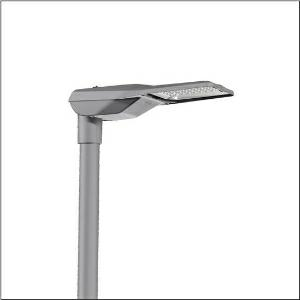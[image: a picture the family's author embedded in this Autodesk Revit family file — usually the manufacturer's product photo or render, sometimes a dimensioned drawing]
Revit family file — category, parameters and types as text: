
# Revit family: streetlight_sl_21_mini___st1_0a_5xe2d33s08gb_0caf
name_source: partatom
category: Lighting Fixtures
units: mm (PartAtom-declared; Revit-internal decimal feet)

## family parameters
Cut with Voids When Loaded = No
Host = Face
Light Source = No
Part Type = Normal
Room Calculation Point = No
Round Connector Dimension = Use Diameter
Shared = No

## types (1)
- --- (1 x LED, 5940 lm, 40.4 W, 3000K)
    Apparent Load = 40 VA
    CIE Flux Codes = 37 72 97 100 100
    Color Rendering = 70
    Color Temperature = 3000K
    Default Elevation = 1800 mm
    Description = Streetlight SL 21 mini, mast luminaire, primary light control with lens, of PMMA, primary optical cover: cover, of toughened safety glass, transparent, light distribution: ST1.0a, light emission: direct distribution, primary light characteristic: asymmetric, installation type: side-entry, post-top, LED, High Power LED, rated luminous flux: 5.940lm, luminous efficacy: 147lm/W, light colour: 730, colour temperature: 3000K, control gear: ECG Smart Interface, control: flexible luminous flux parameterisation, time-dependent luminous flux control, constant luminous flux control, overheat protection, mains connection: 220..240V, AC, 50/60Hz, start of lifetime: 40W, end of lifetime: 41W, reduction: 19W, luminaire housing, of diecast aluminium, powder-coated, Siteco® metallic grey (DB 702S), corrosivity category C5 according to DIN EN ISO 12944, length: 628mm, width: 235mm, height: 110mm, spigot size: 60/76mm (post-top) and 42/60/76mm (side-entry), mast flange for spigot size: 42mm: 5XC10008XM4, 60mm: 5XC10008XM2, 76/60mm: 5XC10108XM1, protection rating (complete): IP66, insulation class (complete): insulation class II (safety insulation), certification: CE, ENEC, VDE, impact resistance: IK09, permissible operating ambient temperature for outdoor applications: -40..+50°C, standard-compliant lighting for roads and squares, packaging unit: 1 piece

Light Distribution: ST1.0a
    Height = 110 mm
    Lamp = 1 x LED
    Lamp Light Flux = 5940 lm
    Lamp Power = 40.4 W
    Lamp count = 1
    Length = 625 mm
    Luminous efficacy = 147 lm/W
    Manufacturer = Siteco
    ModVariant = No
    Model = 5XE2D33S08GB
    Number of Poles = 1
    OnlyDefault = Yes
    Power Factor = 1
    Product Name = Streetlight SL 21 mini | ST1.0a
    Product group = mast luminaire | pylon top
    ProductGroupID = 6100
    Protection Class = Protection class II
    Protection Degree = IP 66
    RLX_Detail_Level = 1
    RlxData = <blob elided: 91809 chars, md5=dd1bda40>
    Socket = socket
    Standby Power = 0 W
    System Light Flux = 5940 lm
    System Power = 40 W
    Type Comments = factory setting: luminous flux: 100 % | dim-lin: 254 | 812 mA
    Type Image = l_1003515.jpg
    URL = http://relux.com
    VarID = @adj_106999
    Voltage = 0 V
    Weight = 0.00 kg
    Width = 234 mm

## geometry (parser evidence)
native form markers: Blend x4, Sweep x12
no freeform markers — native parametric forms only
